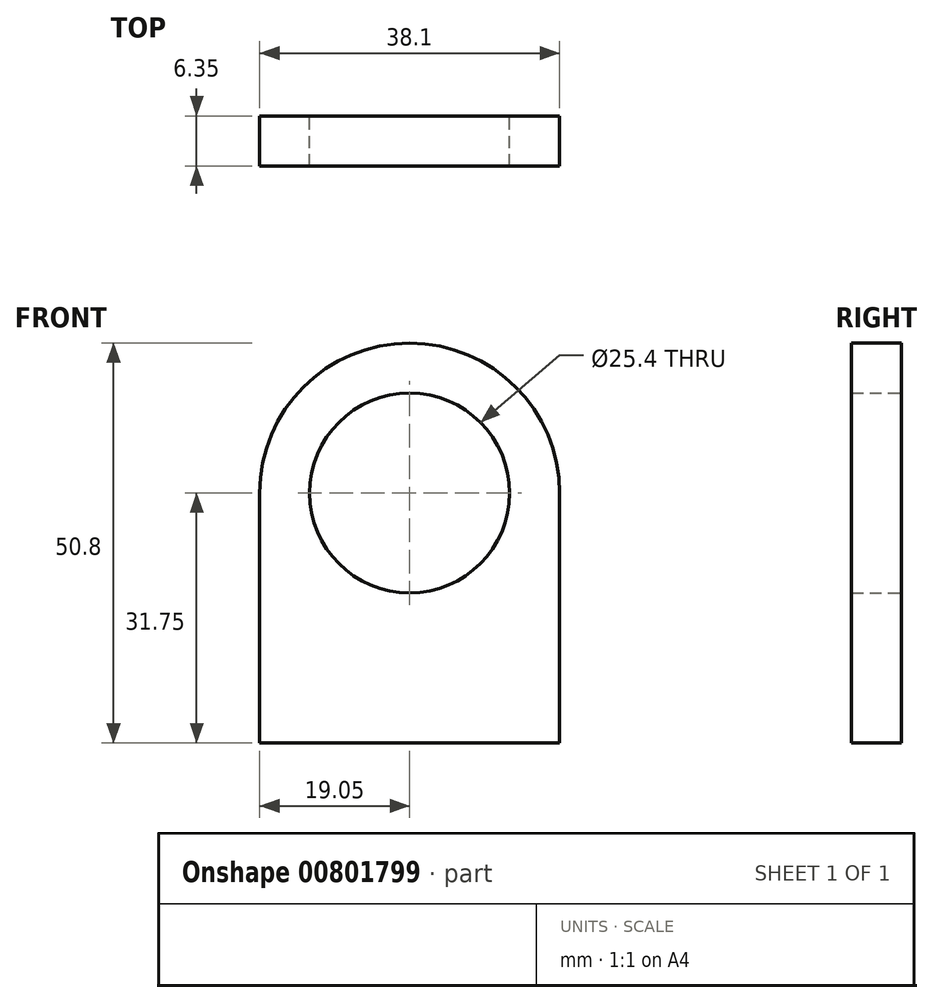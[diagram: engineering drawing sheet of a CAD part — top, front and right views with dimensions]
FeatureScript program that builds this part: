
annotation { "Feature Type Name" : "Feature", "Feature Type Description" : "" }
export const myFeature = defineFeature(function(context is Context, id is Id, definition is map)
    precondition{}
    {
        {
            var Q0;
            Q0=qCreatedBy(makeId("Front.planeOp"),FACE);
            var sketch = newSketch(context, id + "F0", { "sketchPlane" : qUnion([Q0])});
            skLineSegment(sketch, "E0.bottom", {"start": v(19.05, -25.4) * mm, "end": v(-19.05, -25.4) * mm});
            skLineSegment(sketch, "E0.top", {"start": v(0, 25.4) * mm, "end": v(0, 25.4) * mm});
            skLineSegment(sketch, "E0.left", {"start": v(19.05, -25.4) * mm, "end": v(19.05, 6.35) * mm});
            skLineSegment(sketch, "E0.right", {"start": v(-19.05, -25.4) * mm, "end": v(-19.05, 6.35) * mm});
            skPoint(sketch, "E0.middle", {"position": v(0, 0) * mm});
            skCircle(sketch, "E1", {"center": v(0, 6.35) * mm, "radius": 12.7 * mm});
            skPoint(sketch, "E2.visualSharp", {"position": v(-19.05, 25.4) * mm});
            skArc(sketch, "E2.filletArc", {"start": v(0, 25.4) * mm, "mid": v(-13.47, 19.82) * mm, "end": v(-19.05, 6.35) * mm});
            skPoint(sketch, "E3.visualSharp", {"position": v(19.05, 25.4) * mm});
            skArc(sketch, "E3.filletArc", {"start": v(19.05, 6.35) * mm, "mid": v(13.47, 19.82) * mm, "end": v(0, 25.4) * mm});
            skSolve(sketch);
        }
        {
            var Q0;
            Q0=makeQuery(id+"F0.imprint","IMPRINT",FACE,{"disambiguationData":[TD([[makeQuery(id+"F0.imprint","IMPRINT",EDGE,{"derivedFrom":sQuery(id+"F0.wireOp",EDGE,"E0.bottom")}),-1.0]])]});
            extrude(context, id + "F1", {"entities" : qUnion([Q0]), "depth" : 6.35 * mm, "offsetDistance" : 25.4 * mm});
        }
    });
